# Revit family: 401_104ce6e9b0ed4f39abf3e4b8b1c4bf
name_source: partatom
category: Mechanical Equipment
units: mm (PartAtom-declared; Revit-internal decimal feet)

## family parameters
Always vertical = Yes
Classification = None
Cut with Voids When Loaded = No
Part Type = Normal
Room Calculation Point = No
Round Connector Dimension = Use Diameter
Shared = No
Work Plane-Based = No

## types (1)
- Leonardo 5.5 (600x2000) line - Heating - 3 panels
    CAT0 = Yes
    Description = Radiant gypsum panel with internal pipes  and EPS
    E1 = 35 mm  [stored 0.114829 ft]
    E2 = 50 mm  [stored 0.164042 ft]
    H = 500 mm  [stored 1.64042 ft]
    H1 = 25 mm  [stored 0.082021 ft]
    H_ARR = 0 mm  [stored 0 ft]
    L1 = 2000 mm  [stored 6.56168 ft]
    L2 = 2000 mm  [stored 6.56168 ft]
    LL = 3000 mm  [stored 9.84252 ft]
    LX1 = 2000 mm  [stored 6.56168 ft]
    LX2 = 0 mm  [stored 0 ft]
    L_ARR = 400 mm  [stored 1.31234 ft]
    MC Product Code = Leonardo 5.5 (600x2000) line - Heating - 3 panels
    MT1 = No
    MT2 = Yes
    Manufacturer = Eurotherm
    PH = 50 mm  [stored 0.164042 ft]
    PW = 600 mm  [stored 1.9685 ft]
    QmdConnectorList = 331;PD;361;PD
    URL = https://www.eurotherm.info
    V2 = Yes
    V3 = Yes
    W = 500 mm  [stored 1.64042 ft]
    WW = 300 mm  [stored 0.984252 ft]
    W_ARR = 400 mm  [stored 1.31234 ft]
    magiPartTypeId = 401
    magiProductFamilyId = 104ce6e9b0ed4f39abf3e4b8b1c4bf
    magiProductId = 91f1890c15b14077b77ba096434033

note: [stored X ft] marks values corroborated as IEEE doubles in the binary element streams (Revit-internal decimal feet)

## geometry (parser evidence)
native form markers: Sweep x2
no freeform markers — native parametric forms only
